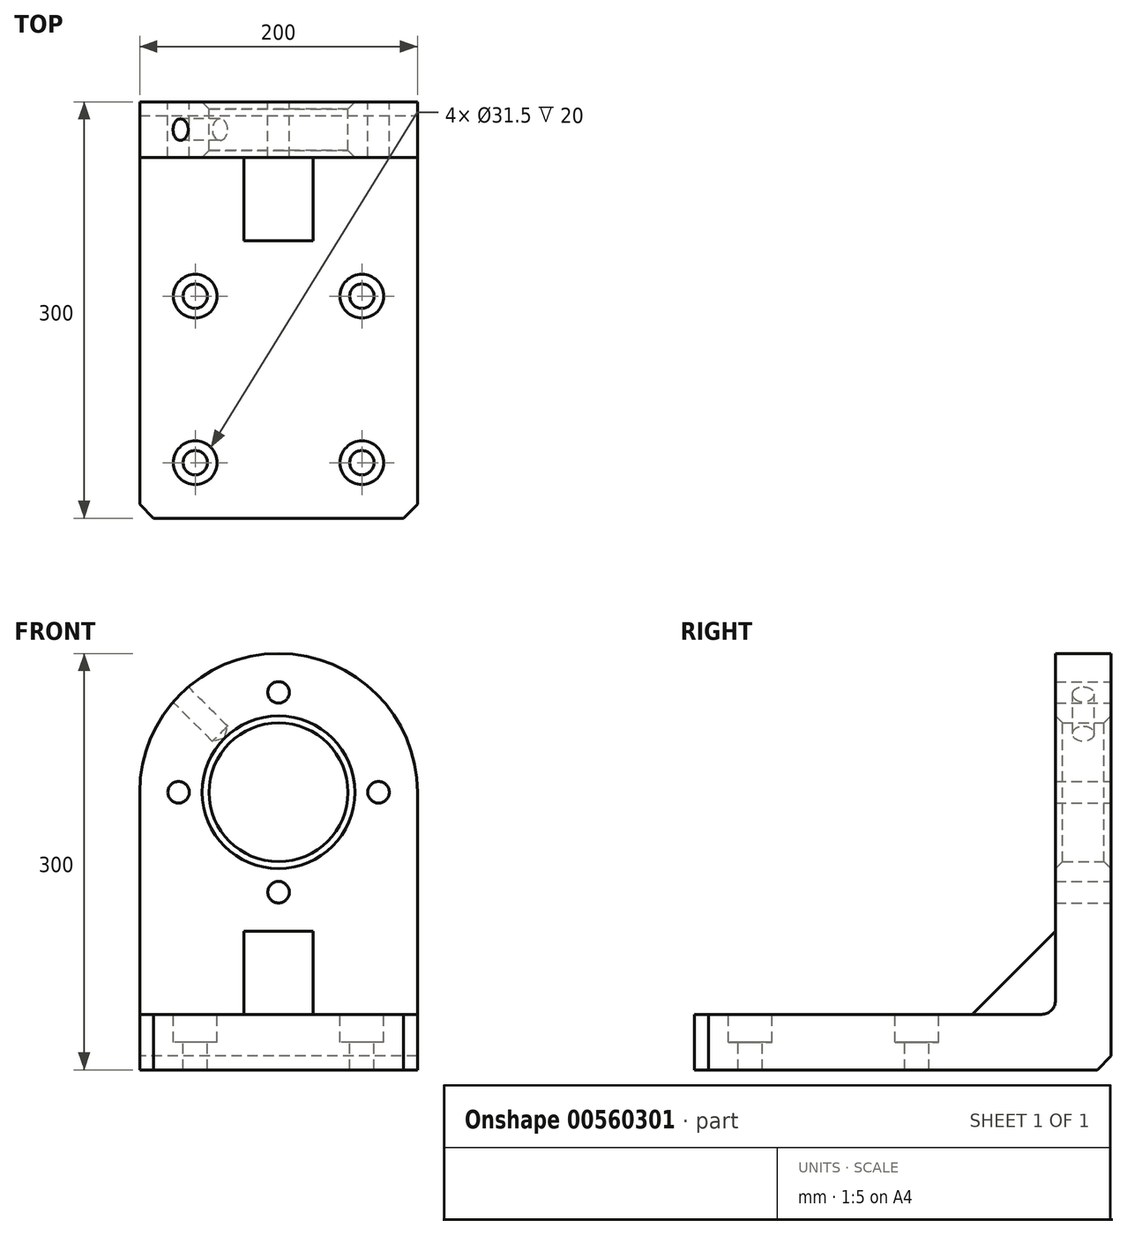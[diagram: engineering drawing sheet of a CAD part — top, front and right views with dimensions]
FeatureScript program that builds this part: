
annotation { "Feature Type Name" : "Feature", "Feature Type Description" : "" }
export const myFeature = defineFeature(function(context is Context, id is Id, definition is map)
    precondition{}
    {
        {
            var Q0;
            Q0=qCreatedBy(makeId("Front.planeOp"),FACE);
            var sketch = newSketch(context, id + "F0", { "sketchPlane" : qUnion([Q0])});
            skLineSegment(sketch, "E0.bottom", {"start": v(-100, 0) * mm, "end": v(100, 0) * mm});
            skLineSegment(sketch, "E0.top", {"start": v(0, 300) * mm, "end": v(0, 300) * mm});
            skLineSegment(sketch, "E0.left", {"start": v(-100, 0) * mm, "end": v(-100, 200) * mm});
            skLineSegment(sketch, "E0.right", {"start": v(100, 0) * mm, "end": v(100, 200) * mm});
            skPoint(sketch, "E1.visualSharp", {"position": v(-100, 300) * mm});
            skArc(sketch, "E1.filletArc", {"start": v(0, 300) * mm, "mid": v(-70.71, 270.71) * mm, "end": v(-100, 200) * mm});
            skPoint(sketch, "E2.visualSharp", {"position": v(100, 300) * mm});
            skArc(sketch, "E2.filletArc", {"start": v(100, 200) * mm, "mid": v(70.71, 270.71) * mm, "end": v(0, 300) * mm});
            skCircle(sketch, "E3", {"center": v(0, 200) * mm, "radius": 50 * mm});
            skCircle(sketch, "E4", {"center": v(0, 200) * mm, "radius": 72 * mm, "construction": true});
            skCircle(sketch, "E5", {"center": v(0, 272) * mm, "radius": 7.58 * mm});
            skCircle(sketch, "E6.1.0", {"center": v(-72, 200) * mm, "radius": 7.58 * mm});
            skCircle(sketch, "E6.2.0", {"center": v(0, 128) * mm, "radius": 7.58 * mm});
            skCircle(sketch, "E6.3.0", {"center": v(72, 200) * mm, "radius": 7.58 * mm});
            skSolve(sketch);
        }
        {
            var Q0;
            Q0 = qSketchRegion(id + "F0", true);
            var Q1;
            Q1=makeQuery(id+"F0.imprint","IMPRINT",FACE,{"disambiguationData":[TD([[makeQuery(id+"F0.imprint","IMPRINT",EDGE,{"derivedFrom":sQuery(id+"F0.wireOp",EDGE,"E6.3.0")}),1.0]])]});
            var Q2;
            Q2=makeQuery(id+"F0.imprint","IMPRINT",FACE,{"disambiguationData":[TD([[makeQuery(id+"F0.imprint","IMPRINT",EDGE,{"derivedFrom":sQuery(id+"F0.wireOp",EDGE,"E6.2.0")}),1.0]])]});
            var Q3;
            Q3=makeQuery(id+"F0.imprint","IMPRINT",FACE,{"disambiguationData":[TD([[makeQuery(id+"F0.imprint","IMPRINT",EDGE,{"derivedFrom":sQuery(id+"F0.wireOp",EDGE,"E6.1.0")}),1.0]])]});
            var Q4;
            Q4=makeQuery(id+"F0.imprint","IMPRINT",FACE,{"disambiguationData":[TD([[makeQuery(id+"F0.imprint","IMPRINT",EDGE,{"derivedFrom":sQuery(id+"F0.wireOp",EDGE,"E5")}),1.0]])]});
            extrude(context, id + "F1", {"entities" : qUnion([Q0, Q1, Q2, Q3, Q4]), "depth" : 40 * mm, "offsetDistance" : 25 * mm});
        }
        {
            var Q0;
            Q0=sQuery(id+"F0.wireOp",VERTEX,"E5.center");
            var Q1;
            Q1=sQuery(id+"F0.wireOp",VERTEX,"E6.3.0.center");
            var Q2;
            Q2=sQuery(id+"F0.wireOp",VERTEX,"E6.2.0.center");
            var Q3;
            Q3=sQuery(id+"F0.wireOp",VERTEX,"E6.1.0.center");
            var Q4;
            Q4=makeQuery(id+"F1.opExtrude","SWEPT_BODY",BODY,{"disambiguationData":[OSD([sQuery(id+"F0.wireOp",EDGE,"E0.bottom"),sQuery(id+"F0.wireOp",EDGE,"E0.left"),sQuery(id+"F0.wireOp",EDGE,"E0.right"),sQuery(id+"F0.wireOp",EDGE,"E1.filletArc"),sQuery(id+"F0.wireOp",EDGE,"E2.filletArc"),sQuery(id+"F0.wireOp",EDGE,"E3")])]});
            hole(context, id + "F2", {"style" : HoleStyle.SIMPLE, "endStyle" : HoleEndStyle.BLIND, "oppositeDirection" : true, "standardTappedOrClearance" : lookupTablePath({ "standard" : "ISO", "fit" : "Normal", "size" : "M14", "type" : "Clearance" }), "standardBlindInLast" : lookupTablePath({ "fit" : "Standard", "standard" : "ISO", "size" : "M14", "type" : "Clearance" }), "holeDiameter" : 15.5 * mm, "holeDepth" : 40 * mm, "isTappedThrough" : true, "tappedDepth" : 12 * mm, "tapClearance" : 3, "locations" : qUnion([Q0, Q1, Q2, Q3]), "scope" : qUnion([Q4])});
        }
        {
            var Q0;
            Q0=makeQuery(id+"F1.opExtrude","CAP_EDGE",EDGE,{"disambiguationData":[OSD([sQuery(id+"F0.wireOp",EDGE,"E3")])],"isStart":true});
            var Q1;
            Q1=makeQuery(id+"F1.opExtrude","CAP_EDGE",EDGE,{"disambiguationData":[OSD([sQuery(id+"F0.wireOp",EDGE,"E3")])],"isStart":false});
            chamfer(context, id + "F3", {"entities" : qUnion([Q0, Q1]), "width" : 5 * mm, "tangentPropagation" : true});
        }
        {
            var Q0;
            Q0=makeQuery(id+"F0.imprint","IMPRINT",FACE,{"disambiguationData":[TD([[makeQuery(id+"F0.imprint","IMPRINT",EDGE,{"derivedFrom":sQuery(id+"F0.wireOp",EDGE,"E0.bottom")}),1.0]])]});
            cPlane(context, id + "F4", {"entities" : qUnion([Q0]), "cplaneType" : CPlaneType.OFFSET, "offset" : 20 * mm, "width" : 150 * mm, "height" : 150 * mm});
        }
        {
            var Q0;
            Q0=qCreatedBy(id+"F4.planeOp",FACE);
            var sketch = newSketch(context, id + "F5", { "sketchPlane" : qUnion([Q0])});
            skLineSegment(sketch, "E7.0.0", {"start": v(100, 0) * mm, "end": v(100, 200) * mm});
            skArc(sketch, "E7.0.1", {"start": v(100, 200) * mm, "mid": v(0, 300) * mm, "end": v(-100, 200) * mm});
            skLineSegment(sketch, "E7.0.2", {"start": v(-100, 200) * mm, "end": v(-100, 0) * mm});
            skLineSegment(sketch, "E7.0.3", {"start": v(-100, 0) * mm, "end": v(100, 0) * mm});
            skCircle(sketch, "E8.0", {"center": v(0, 200) * mm, "radius": 72 * mm});
            skLineSegment(sketch, "E9", {"start": v(0, 200) * mm, "end": v(100, 200) * mm, "construction": true});
            skLineSegment(sketch, "E10", {"start": v(0, 200) * mm, "end": v(70.71, 270.71) * mm});
            skLineSegment(sketch, "E11", {"start": v(0, 318.05) * mm, "end": v(0, 62) * mm, "construction": true});
            skPoint(sketch, "E11.startSnap0", {"position": v(0, 300) * mm});
            skLineSegment(sketch, "E12.MirrorCS", {"start": v(0, 200) * mm, "end": v(-70.71, 270.71) * mm});
            skSolve(sketch);
        }
        {
            var Q0;
            Q0=sQuery(id+"F5.wireOp",EDGE,"E12.MirrorCS");
            var Q1;
            Q1=sQuery(id+"F5.wireOp",VERTEX,"E12.MirrorCS.end");
            cPlane(context, id + "F6", {"entities" : qUnion([Q0, Q1]), "cplaneType" : CPlaneType.LINE_POINT, "offset" : 25 * mm, "width" : 150 * mm, "height" : 150 * mm});
        }
        {
            var Q0;
            Q0=sQuery(id+"F5.wireOp",EDGE,"E10");
            var Q1;
            Q1=sQuery(id+"F5.wireOp",VERTEX,"E10.end");
            cPlane(context, id + "F7", {"entities" : qUnion([Q0, Q1]), "cplaneType" : CPlaneType.LINE_POINT, "offset" : 25 * mm, "width" : 150 * mm, "height" : 150 * mm});
        }
        {
            var Q0;
            Q0=qCreatedBy(id+"F7.planeOp",FACE);
            var sketch = newSketch(context, id + "F8", { "sketchPlane" : qUnion([Q0])});
            skPoint(sketch, "E13.0", {"position": v(-141.42, -20) * mm});
            skSolve(sketch);
        }
        {
            var Q0;
            Q0=sQuery(id+"F8.wireOp",VERTEX,"E13.0");
            var Q1;
            Q1=makeQuery(id+"F1.opExtrude","SWEPT_BODY",BODY,{"disambiguationData":[OSD([sQuery(id+"F0.wireOp",EDGE,"E0.bottom"),sQuery(id+"F0.wireOp",EDGE,"E0.left"),sQuery(id+"F0.wireOp",EDGE,"E0.right"),sQuery(id+"F0.wireOp",EDGE,"E1.filletArc"),sQuery(id+"F0.wireOp",EDGE,"E2.filletArc"),sQuery(id+"F0.wireOp",EDGE,"E3")])]});
            hole(context, id + "F9", {"style" : HoleStyle.SIMPLE, "endStyle" : HoleEndStyle.BLIND, "standardTappedOrClearance" : lookupTablePath({ "standard" : "ISO", "fit" : "Normal", "size" : "M14", "type" : "Clearance" }), "standardBlindInLast" : lookupTablePath({ "fit" : "Standard", "standard" : "ISO", "size" : "M14", "type" : "Clearance" }), "holeDiameter" : 15.5 * mm, "holeDepth" : 40 * mm, "isTappedThrough" : true, "tappedDepth" : 12 * mm, "tapClearance" : 3, "locations" : qUnion([Q0]), "scope" : qUnion([Q1])});
        }
        {
            var Q0;
            Q0=qCreatedBy(id+"F6.planeOp",FACE);
            var sketch = newSketch(context, id + "F10", { "sketchPlane" : qUnion([Q0])});
            skPoint(sketch, "E14.0", {"position": v(20, 141.42) * mm});
            skSolve(sketch);
        }
        {
            var Q0;
            Q0=sQuery(id+"F10.wireOp",VERTEX,"E14.0");
            var Q1;
            Q1=makeQuery(id+"F1.opExtrude","SWEPT_BODY",BODY,{"disambiguationData":[OSD([sQuery(id+"F0.wireOp",EDGE,"E0.bottom"),sQuery(id+"F0.wireOp",EDGE,"E0.left"),sQuery(id+"F0.wireOp",EDGE,"E0.right"),sQuery(id+"F0.wireOp",EDGE,"E1.filletArc"),sQuery(id+"F0.wireOp",EDGE,"E2.filletArc"),sQuery(id+"F0.wireOp",EDGE,"E3")])]});
            hole(context, id + "F11", {"style" : HoleStyle.SIMPLE, "endStyle" : HoleEndStyle.BLIND, "standardTappedOrClearance" : lookupTablePath({ "standard" : "ISO", "fit" : "Normal", "size" : "M14", "type" : "Clearance" }), "standardBlindInLast" : lookupTablePath({ "fit" : "Standard", "standard" : "ISO", "size" : "M14", "type" : "Clearance" }), "holeDiameter" : 15.5 * mm, "holeDepth" : 40 * mm, "isTappedThrough" : true, "tappedDepth" : 12 * mm, "tapClearance" : 3, "locations" : qUnion([Q0]), "scope" : qUnion([Q1])});
        }
        {
            var Q0;
            Q0=qCreatedBy(makeId("Right.planeOp"),FACE);
            var sketch = newSketch(context, id + "F12", { "sketchPlane" : qUnion([Q0])});
            skLineSegment(sketch, "E15.bottom", {"start": v(0, 0) * mm, "end": v(-300, 0) * mm});
            skLineSegment(sketch, "E15.top", {"start": v(0, 40) * mm, "end": v(-300, 40) * mm});
            skLineSegment(sketch, "E15.left", {"start": v(0, 0) * mm, "end": v(0, 40) * mm});
            skLineSegment(sketch, "E15.right", {"start": v(-300, 0) * mm, "end": v(-300, 40) * mm});
            skSolve(sketch);
        }
        {
            var Q0;
            Q0 = qSketchRegion(id + "F12", true);
            extrude(context, id + "F13", {"entities" : qUnion([Q0]), "operationType" : NewBodyOperationType.ADD, "endBound" : BoundingType.SYMMETRIC, "depth" : 200 * mm, "offsetDistance" : 25 * mm});
        }
        {
            var Q0;
            Q0=qCreatedBy(makeId("Right.planeOp"),FACE);
            var sketch = newSketch(context, id + "F14", { "sketchPlane" : qUnion([Q0])});
            skPoint(sketch, "E16.0", {"position": v(-40, 40) * mm});
            skLineSegment(sketch, "E17", {"start": v(-40, 100) * mm, "end": v(-100, 40) * mm});
            skLineSegment(sketch, "E18", {"start": v(-40, 100) * mm, "end": v(-40, 40) * mm});
            skLineSegment(sketch, "E19", {"start": v(-40, 40) * mm, "end": v(-100, 40) * mm});
            skSolve(sketch);
        }
        {
            var Q0;
            Q0=makeQuery(id+"F13.boolean.opBoolean","INTERSECT",EDGE,{"derivedFrom":[makeQuery(id+"F1.opExtrude","CAP_FACE",FACE,{"disambiguationData":[OSD([sQuery(id+"F0.wireOp",EDGE,"E0.bottom"),sQuery(id+"F0.wireOp",EDGE,"E0.left"),sQuery(id+"F0.wireOp",EDGE,"E0.right"),sQuery(id+"F0.wireOp",EDGE,"E1.filletArc"),sQuery(id+"F0.wireOp",EDGE,"E2.filletArc"),sQuery(id+"F0.wireOp",EDGE,"E3")])],"isStart":false}),makeQuery(id+"F13.opExtrude","SWEPT_FACE",FACE,{"disambiguationData":[OSD([sQuery(id+"F12.wireOp",EDGE,"E15.top")])]})]});
            fillet(context, id + "F15", {"entities" : qUnion([Q0]), "radius" : 10 * mm, "tangentPropagation" : true, "allowEdgeOverflow" : false});
        }
        {
            var Q0;
            Q0 = qSketchRegion(id + "F14", true);
            extrude(context, id + "F16", {"entities" : qUnion([Q0]), "operationType" : NewBodyOperationType.ADD, "endBound" : BoundingType.SYMMETRIC, "depth" : 50 * mm, "offsetDistance" : 25 * mm});
        }
        {
            var Q0;
            Q0=makeQuery(id+"F13.opExtrude","CAP_EDGE",EDGE,{"disambiguationData":[OSD([sQuery(id+"F12.wireOp",EDGE,"E15.right")])],"isStart":false});
            var Q1;
            Q1=makeQuery(id+"F13.opExtrude","CAP_EDGE",EDGE,{"disambiguationData":[OSD([sQuery(id+"F12.wireOp",EDGE,"E15.right")])],"isStart":true});
            var Q2;
            Q2=makeQuery(id+"F1.opExtrude","CAP_EDGE",EDGE,{"disambiguationData":[OSD([sQuery(id+"F0.wireOp",EDGE,"E0.bottom")])],"isStart":true});
            chamfer(context, id + "F17", {"entities" : qUnion([Q0, Q1, Q2]), "width" : 10 * mm, "tangentPropagation" : true});
        }
        {
            var Q0;
            Q0=makeQuery(id+"F13.opExtrude","SWEPT_FACE",FACE,{"disambiguationData":[OSD([sQuery(id+"F12.wireOp",EDGE,"E15.top")])]});
            var sketch = newSketch(context, id + "F18", { "sketchPlane" : qUnion([Q0])});
            skCircle(sketch, "E20", {"center": v(-60, -140) * mm, "radius": 13.45 * mm, "construction": true});
            skLineSegment(sketch, "E21.0", {"start": v(0, 0) * mm, "end": v(0, -300) * mm});
            skCircle(sketch, "E22.1.0", {"center": v(-60, -260) * mm, "radius": 13.45 * mm, "construction": true});
            skCircle(sketch, "E22.2.0", {"center": v(60, -260) * mm, "radius": 13.45 * mm, "construction": true});
            skCircle(sketch, "E22.3.0", {"center": v(60, -140) * mm, "radius": 13.45 * mm, "construction": true});
            skPoint(sketch, "E22.center", {"position": v(0, -200) * mm});
            skSolve(sketch);
        }
        {
            var Q0;
            Q0=sQuery(id+"F18.wireOp",VERTEX,"E20.center");
            var Q1;
            Q1=sQuery(id+"F18.wireOp",VERTEX,"E22.3.0.center");
            var Q2;
            Q2=sQuery(id+"F18.wireOp",VERTEX,"E22.2.0.center");
            var Q3;
            Q3=sQuery(id+"F18.wireOp",VERTEX,"E22.1.0.center");
            var Q4;
            Q4=makeQuery(id+"F1.opExtrude","SWEPT_BODY",BODY,{"disambiguationData":[OSD([sQuery(id+"F0.wireOp",EDGE,"E0.bottom"),sQuery(id+"F0.wireOp",EDGE,"E0.left"),sQuery(id+"F0.wireOp",EDGE,"E0.right"),sQuery(id+"F0.wireOp",EDGE,"E1.filletArc"),sQuery(id+"F0.wireOp",EDGE,"E2.filletArc"),sQuery(id+"F0.wireOp",EDGE,"E3")])]});
            hole(context, id + "F19", {"style" : HoleStyle.C_BORE, "endStyle" : HoleEndStyle.THROUGH, "holeDiameter" : 17.5 * mm, "cBoreDiameter" : 31.5 * mm, "cBoreDepth" : 20 * mm, "isTappedThrough" : true, "tappedDepth" : 12 * mm, "tapClearance" : 3, "locations" : qUnion([Q0, Q1, Q2, Q3]), "scope" : qUnion([Q4])});
        }
    });
